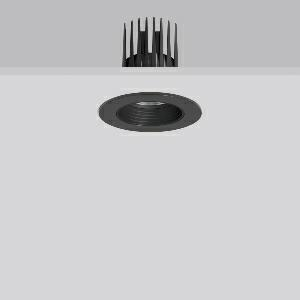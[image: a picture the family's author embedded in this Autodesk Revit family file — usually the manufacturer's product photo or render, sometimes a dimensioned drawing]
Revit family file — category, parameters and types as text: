
# Revit family: heledon_mini_e_901754_003_2_282c
name_source: partatom
category: Lighting Fixtures
units: mm (PartAtom-declared; Revit-internal decimal feet)

## family parameters
Cut with Voids When Loaded = No
Host = Face
Light Source = No
Part Type = Normal
Room Calculation Point = No
Round Connector Dimension = Use Diameter
Shared = No

## types (1)
- HELEDON mini E (1 x LED Modul 927, 3050 lm, 2700)
    Apparent Load = 29 VA
    Approval mark = CE
    CIE Flux Codes = 80 99 100 100 100
    Color Rendering = 92
    Color Temperature = 2700
    Default Elevation = 1800 mm
    Description = Series: HELEDON mini
Round recessed downlight. Housing: die-cast aluminium, powder-coated. Black plastic ring and recessed LED to prevent glare from the side. Optical assembly with lens made of plastic (polycarbonate) for the best homogeneous light distribution - can be changed without tools. Best colour rendering index Ra>90. Suitable for Recessed ceiling mounting. Installation without tools thanks to spring fastening system. Including separate LED converter with connecting cable 600 mm.High quality converter without flickering and stroboscopic effect. Through-wiring box (5 pole) available as accessory. The following accessories can be mounted without use of tools: interchangeable lenses, decorative glasses, honeycomb louvre, clear and frosted diffusers, white interchangeable plastic ring. 
Colour: deep black, matt (RAL 9005)
Diameter: 124 mm
Height: 3 mm
Cut-out diameter: 114 mm
Recess height: 170 mm
Luminaire: recess height: 120 mm
Lamp: LED
Socket: without socket
Colour temperature: 2700K
Colour rendering index (CRI): 92
System power: 29 W
Rated luminous flux: 3050 lm
Luminous efficiency: 105 lm/W
Control gear: Regulated power supply
Protection class: II
Type of protection: IP 20
    Height = 0 mm  [stored 0 ft]
    Lamp = 1 x LED Modul 927
    Lamp Light Flux = 3050 lm
    Lamp count = 1
    Length = 124 mm  [stored 0.406824 ft]
    Lifetime = 50000 h
    Luminous efficacy = 105 lm/W
    Manufacturer = RZB
    ModVariant = No
    Model = 901754.003.2
    Mounting Place = Ceiling
    Mounting Type = Recessed
    Number of Poles = 1
    OnlyDefault = Yes
    Power Factor = 1
    Product Name = HELEDON mini E
    Product group = Recessed downlights
    ProductGroupID = 402
    Protection Class = Protection class II
    Protection Degree = IP 20
    RLX_Detail_Level = 1
    RLX_Emergency_Light_Flux = 0 lm
    RLX_Emergency_Type = 0
    RLX_Emergency_Type_DB = No
    RlxData = <blob elided: 124441 chars, md5=96948aa5>
    Socket = socket
    Standby Power = 0 W
    System Light Flux = 3050 lm
    System Power = 29 W
    Type Comments = Product without accessories
    Type Image = 901656.003.jpg
    URL = http://relux.com
    VarID = ---
    Voltage = 230 V
    Voltage Range = 220-240 V
    Weight = 0.00 kg
    Width = 0 mm  [stored 0 ft]

note: [stored X ft] marks values corroborated as IEEE doubles in the binary element streams (Revit-internal decimal feet)

## geometry (parser evidence)
native form markers: Blend x4, Sweep x12
no freeform markers — native parametric forms only
